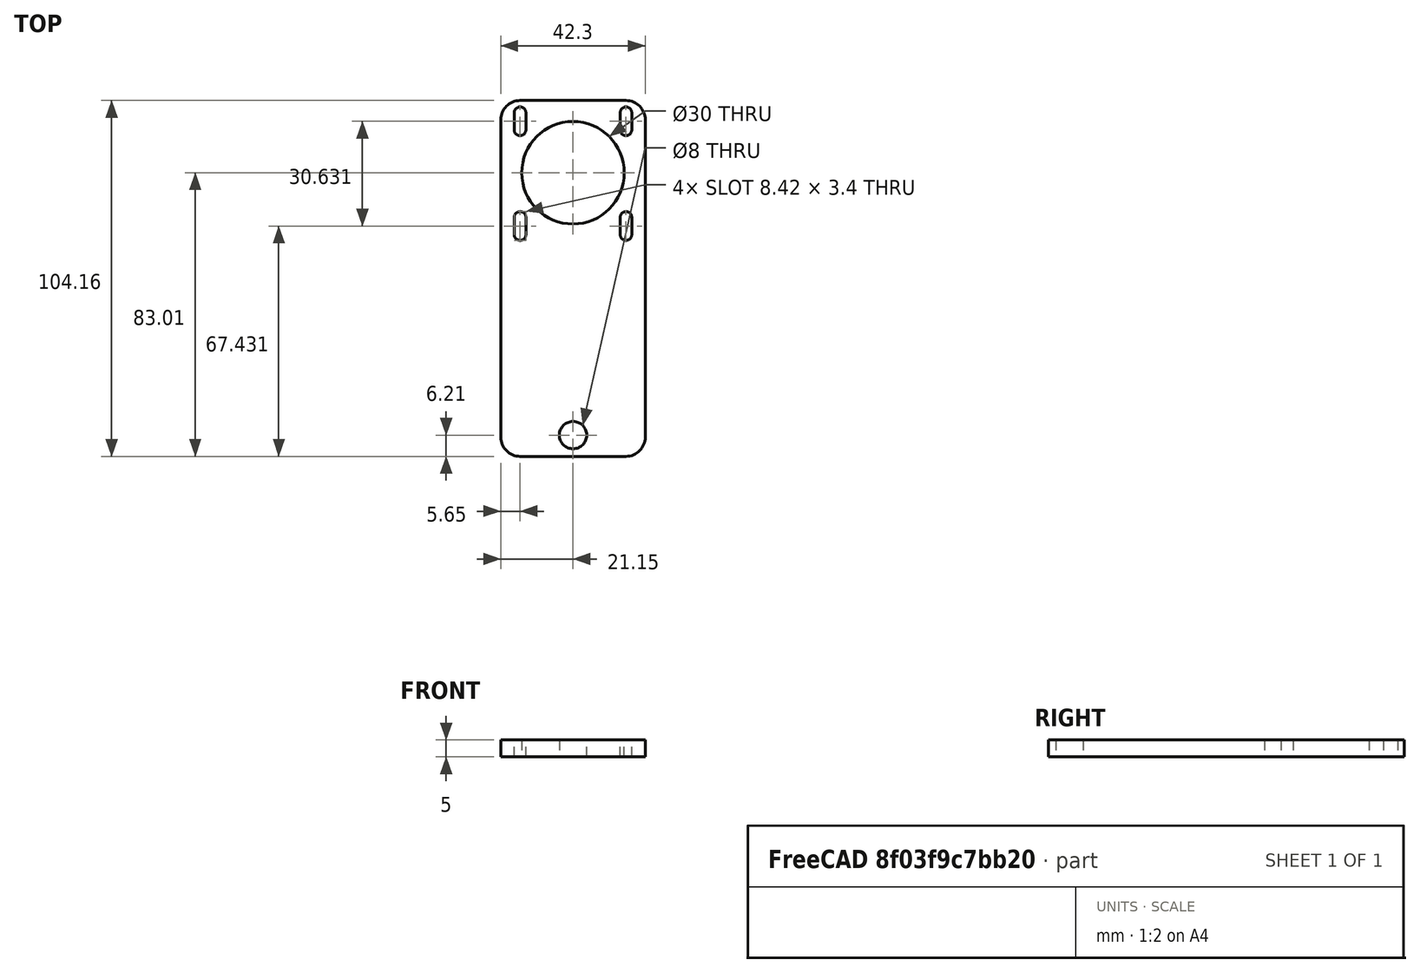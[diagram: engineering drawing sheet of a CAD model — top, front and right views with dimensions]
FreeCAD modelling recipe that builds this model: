
FCSTD DOCUMENT  (FreeCAD 0.16R6706 (Git))
Label: new_bear_stepper_base
License: All rights reserved
LicenseURL: http://en.wikipedia.org/wiki/All_rights_reserved
objects: Sketcher::SketchObject×1, PartDesign::Pad×1
note: 3 computed .brp shape members not serialized (recipe doc carries the construction recipe); baked Part::Feature solids carry a one-line shape summary decoded from their .brp

FEATURE [Sketcher::SketchObject] Sketch
  sketch-geometry (33):
    g0: LineSegment [constr] StartX=-15.5 StartY=15.5 StartZ=0 EndX=15.5 EndY=15.5 EndZ=0
    g1: LineSegment [constr] StartX=15.5 StartY=15.5 StartZ=0 EndX=15.5 EndY=-15.5 EndZ=0
    g2: LineSegment [constr] StartX=15.5 StartY=-15.5 StartZ=0 EndX=-15.5 EndY=-15.5 EndZ=0
    g3: LineSegment [constr] StartX=-15.5 StartY=-15.5 StartZ=0 EndX=-15.5 EndY=15.5 EndZ=0
    g4: LineSegment StartX=-15.5 StartY=21.15 StartZ=0 EndX=15.5 EndY=21.15 EndZ=0
    g5: LineSegment StartX=21.15 StartY=15.5 StartZ=0 EndX=21.15 EndY=-77.3624 EndZ=0
    g6: LineSegment StartX=15.5 StartY=-83.0124 StartZ=0 EndX=-15.5 EndY=-83.0124 EndZ=0
    g7: LineSegment StartX=-21.15 StartY=-77.3624 StartZ=0 EndX=-21.15 EndY=15.5 EndZ=0
    g8: LineSegment [constr] StartX=15.5 StartY=15.5 StartZ=0 EndX=15.5 EndY=21.15 EndZ=0
    g9: LineSegment [constr] StartX=15.5 StartY=15.5 StartZ=0 EndX=21.15 EndY=15.5 EndZ=0
    g10: Circle CenterX=0 CenterY=-76.8 CenterZ=0 NormalX=0 NormalY=0 NormalZ=1 Radius=4
    g11: Circle CenterX=0 CenterY=0 CenterZ=0 NormalX=0 NormalY=0 NormalZ=1 Radius=15
    g12: LineSegment [constr] StartX=-15.5 StartY=15.5 StartZ=0 EndX=-21.15 EndY=15.5 EndZ=0
    g13: ArcOfCircle CenterX=-15.5 CenterY=-77.3624 CenterZ=0 NormalX=0 NormalY=0 NormalZ=1 Radius=5.65 StartAngle=3.14159 EndAngle=4.71239
    g14: ArcOfCircle CenterX=15.5 CenterY=-77.3624 CenterZ=0 NormalX=0 NormalY=0 NormalZ=1 Radius=5.65 StartAngle=4.71239 EndAngle=6.28319
    g15: ArcOfCircle CenterX=15.5 CenterY=15.5 CenterZ=0 NormalX=0 NormalY=0 NormalZ=1 Radius=5.65 StartAngle=0 EndAngle=1.5708
    g16: ArcOfCircle CenterX=-15.5 CenterY=15.5 CenterZ=0 NormalX=0 NormalY=0 NormalZ=1 Radius=5.65 StartAngle=1.5708 EndAngle=3.14159
    g17: ArcOfCircle CenterX=-15.5 CenterY=12.542 CenterZ=0 NormalX=0 NormalY=0 NormalZ=1 Radius=1.7 StartAngle=3.14159 EndAngle=6.28319
    g18: ArcOfCircle CenterX=-15.5 CenterY=17.5628 CenterZ=0 NormalX=0 NormalY=0 NormalZ=1 Radius=1.7 StartAngle=0 EndAngle=3.14159
    g19: LineSegment StartX=-13.8 StartY=12.542 StartZ=0 EndX=-13.8 EndY=17.5628 EndZ=0
    g20: LineSegment StartX=-17.2 StartY=12.542 StartZ=0 EndX=-17.2 EndY=17.5628 EndZ=0
    g21: ArcOfCircle CenterX=15.5 CenterY=12.542 CenterZ=0 NormalX=0 NormalY=0 NormalZ=1 Radius=1.7 StartAngle=3.14159 EndAngle=6.28319
    g22: ArcOfCircle CenterX=15.5 CenterY=17.5628 CenterZ=0 NormalX=0 NormalY=0 NormalZ=1 Radius=1.7 StartAngle=0 EndAngle=3.14159
    g23: LineSegment StartX=17.2 StartY=12.542 StartZ=0 EndX=17.2 EndY=17.5628 EndZ=0
    g24: LineSegment StartX=13.8 StartY=12.542 StartZ=0 EndX=13.8 EndY=17.5628 EndZ=0
    g25: ArcOfCircle CenterX=-15.5 CenterY=-13.0685 CenterZ=0 NormalX=0 NormalY=0 NormalZ=1 Radius=1.7 StartAngle=0 EndAngle=3.14159
    g26: ArcOfCircle CenterX=-15.5 CenterY=-18.0893 CenterZ=0 NormalX=0 NormalY=0 NormalZ=1 Radius=1.7 StartAngle=3.14159 EndAngle=6.28319
    g27: LineSegment StartX=-17.2 StartY=-13.0685 StartZ=0 EndX=-17.2 EndY=-18.0893 EndZ=0
    g28: LineSegment StartX=-13.8 StartY=-13.0685 StartZ=0 EndX=-13.8 EndY=-18.0893 EndZ=0
    g29: ArcOfCircle CenterX=15.5 CenterY=-13.0685 CenterZ=0 NormalX=0 NormalY=0 NormalZ=1 Radius=1.7 StartAngle=0 EndAngle=3.14159
    g30: ArcOfCircle CenterX=15.5 CenterY=-18.0893 CenterZ=0 NormalX=0 NormalY=0 NormalZ=1 Radius=1.7 StartAngle=3.14159 EndAngle=6.28319
    g31: LineSegment StartX=13.8 StartY=-13.0685 StartZ=0 EndX=13.8 EndY=-18.0893 EndZ=0
    g32: LineSegment StartX=17.2 StartY=-13.0685 StartZ=0 EndX=17.2 EndY=-18.0893 EndZ=0
  constraints (83):
    c: Coincident(g0,g1)
    c: Coincident(g1,g2)
    c: Coincident(g2,g3)
    c: Coincident(g3,g0)
    c: Horizontal(g0)
    c: Horizontal(g2)
    c: Vertical(g1)
    c: Vertical(g3)
    c: DistanceX(g0,g0) = 31
    c: Equal(g1,g0)
    c: Symmetric(g0,g2,g-1)
    c: Horizontal(g4)
    c: Horizontal(g6)
    c: Vertical(g5)
    c: Vertical(g7)
    c: Coincident(g8,g0)
    c: PointOnObject(g8,g4)
    c: Vertical(g8)
    c: Coincident(g9,g0)
    c: PointOnObject(g9,g5)
    c: Horizontal(g9)
    c: Equal(g9,g8)
    c: Radius(g10) = 4
    c: PointOnObject(g10,g-2)
    c: DistanceY(g10,g-1) = 76.8
    c: Coincident(g11,g-1)
    c: Radius(g11) = 15
    c: Coincident(g12,g0)
    c: Horizontal(g12)
    c: Equal(g12,g9)
    c: PointOnObject(g12,g7)
    c: Tangent(g6,g13) = 1.5708
    c: Tangent(g7,g13) = 1.5708
    c: Tangent(g5,g14) = 1.5708
    c: Tangent(g6,g14) = 1.5708
    c: Tangent(g4,g15) = 1.5708
    c: Tangent(g5,g15) = 1.5708
    c: Tangent(g4,g16) = 1.5708
    c: Tangent(g7,g16) = 1.5708
    c: Equal(g16,g15)
    c: Equal(g15,g13)
    c: Equal(g13,g14)
    c: Coincident(g7,g12)
    c: DistanceX(g7,g5) = 42.3
    c: Tangent(g17,g20) = 1.5708
    c: Tangent(g17,g19) = -1.5708
    c: Tangent(g19,g18) = -1.5708
    c: Tangent(g20,g18) = 1.5708
    c: Vertical(g19)
    c: Equal(g17,g18)
    c: PointOnObject(g17,g3)
    c: Radius(g17) = 1.7
    c: Tangent(g21,g24) = 1.5708
    c: Tangent(g21,g23) = -1.5708
    c: Tangent(g23,g22) = -1.5708
    c: Tangent(g24,g22) = 1.5708
    c: Vertical(g23)
    c: Equal(g21,g22)
    c: PointOnObject(g21,g1)
    c: Radius(g21) = 1.7
    c: DistanceY(g18,g22) = 0
    c: Tangent(g25,g28) = 1.5708
    c: Tangent(g25,g27) = -1.5708
    c: Tangent(g27,g26) = -1.5708
    c: Tangent(g28,g26) = 1.5708
    c: Vertical(g27)
    c: Equal(g25,g26)
    c: PointOnObject(g25,g3)
    c: Radius(g26) = 1.7
    c: Tangent(g29,g32) = 1.5708
    c: Tangent(g29,g31) = -1.5708
    c: Tangent(g31,g30) = -1.5708
    c: Tangent(g32,g30) = 1.5708
    c: Vertical(g31)
    c: Equal(g29,g30)
    c: Radius(g30) = 1.7
    c: PointOnObject(g29,g1)
    c: DistanceY(g30,g26) = 0
    c: DistanceY(g29,g25) = 0
    c: DistanceY(g17,g21) = 0
    c: Equal(g31,g28)
    c: Equal(g28,g19)
    c: Equal(g19,g24)
FEATURE [PartDesign::Pad] Pad
  Length = 5
  Length2 = 100
  Sketch = -> Sketch
  Type = 0
